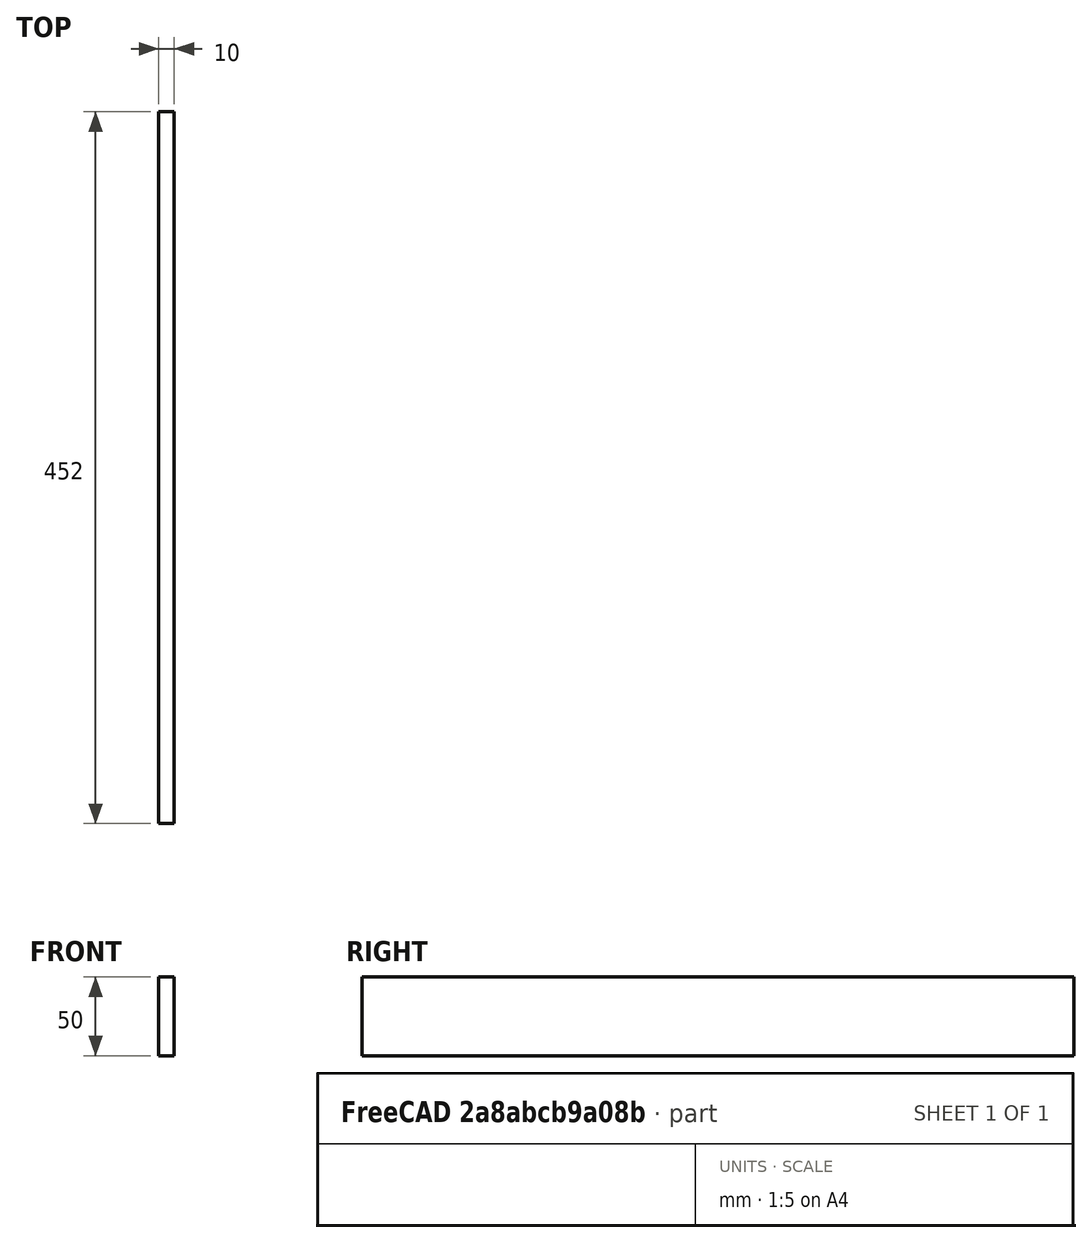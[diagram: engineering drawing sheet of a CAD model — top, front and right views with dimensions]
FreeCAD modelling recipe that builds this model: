
FCSTD DOCUMENT  (FreeCAD 0.18R16131 (Git))
Label: 500_Back_Horizontal_Top
License: All rights reserved
LicenseURL: http://en.wikipedia.org/wiki/All_rights_reserved
objects: Sketcher::SketchObject×1, Spreadsheet::Sheet×1, PartDesign::Pad×1, PartDesign::Body×1
note: 4 computed .brp shape members not serialized (recipe doc carries the construction recipe); baked Part::Feature solids carry a one-line shape summary decoded from their .brp

FEATURE [Sketcher::SketchObject] Sketch
  MapMode = 4
  Placement = pos=(0,0,0) rot=(0.57735,0.57735,0.57735;2.0944rad)
  Support = -> [XY_Plane]
  expr: Constraints[6] = Spreadsheet.nY
  expr: Constraints[5] = Spreadsheet.nZ
  sketch-geometry (5):
    g0: LineSegment StartX=0 StartY=0 StartZ=0 EndX=0 EndY=50 EndZ=0
    g1: LineSegment StartX=452 StartY=0 StartZ=0 EndX=452 EndY=50 EndZ=0
    g2: LineSegment StartX=452 StartY=50 StartZ=0 EndX=0 EndY=50 EndZ=0
    g3: LineSegment StartX=226 StartY=0 StartZ=0 EndX=0 EndY=0 EndZ=0
    g4: LineSegment StartX=452 StartY=0 StartZ=0 EndX=226 EndY=0 EndZ=0
  constraints (14):
    c: Vertical(g0)
    c: Vertical(g1)
    c: Coincident(g2,g1)
    c: Coincident(g2,g0)
    c: Horizontal(g2)
    c: DistanceY(g1,g1) = 50
    c: DistanceX(g2,g2) = 452
    c: Coincident(g3,g0)
    c: Coincident(g4,g1)
    c: Horizontal(g4)
    c: Equal(g3,g4)
    c: Coincident(g4,g3)
    c: Horizontal(g3)
    c: Coincident(g0,g-1)
FEATURE [Spreadsheet::Sheet] Spreadsheet  label="xls"
  cells = B7=KEYBOARD FRONT; B8=Width; C8=nY; D8(nY)==500 - 19 - 19 - 10; B9=Height; C9=nZ; D9(nZ)=50; E9=F(T); B10=Thickness; C10=nT; D10(nT)=10
FEATURE [PartDesign::Pad] Pad
  Length = 10
  Length2 = 100
  Profile = -> Sketch
  Reversed = true
  Type = 0
  expr: Length = Spreadsheet.nT
FEATURE [PartDesign::Body] Body
  Group = -> [Sketch,Pad]
  Origin = -> Origin
  Tip = -> Pad
